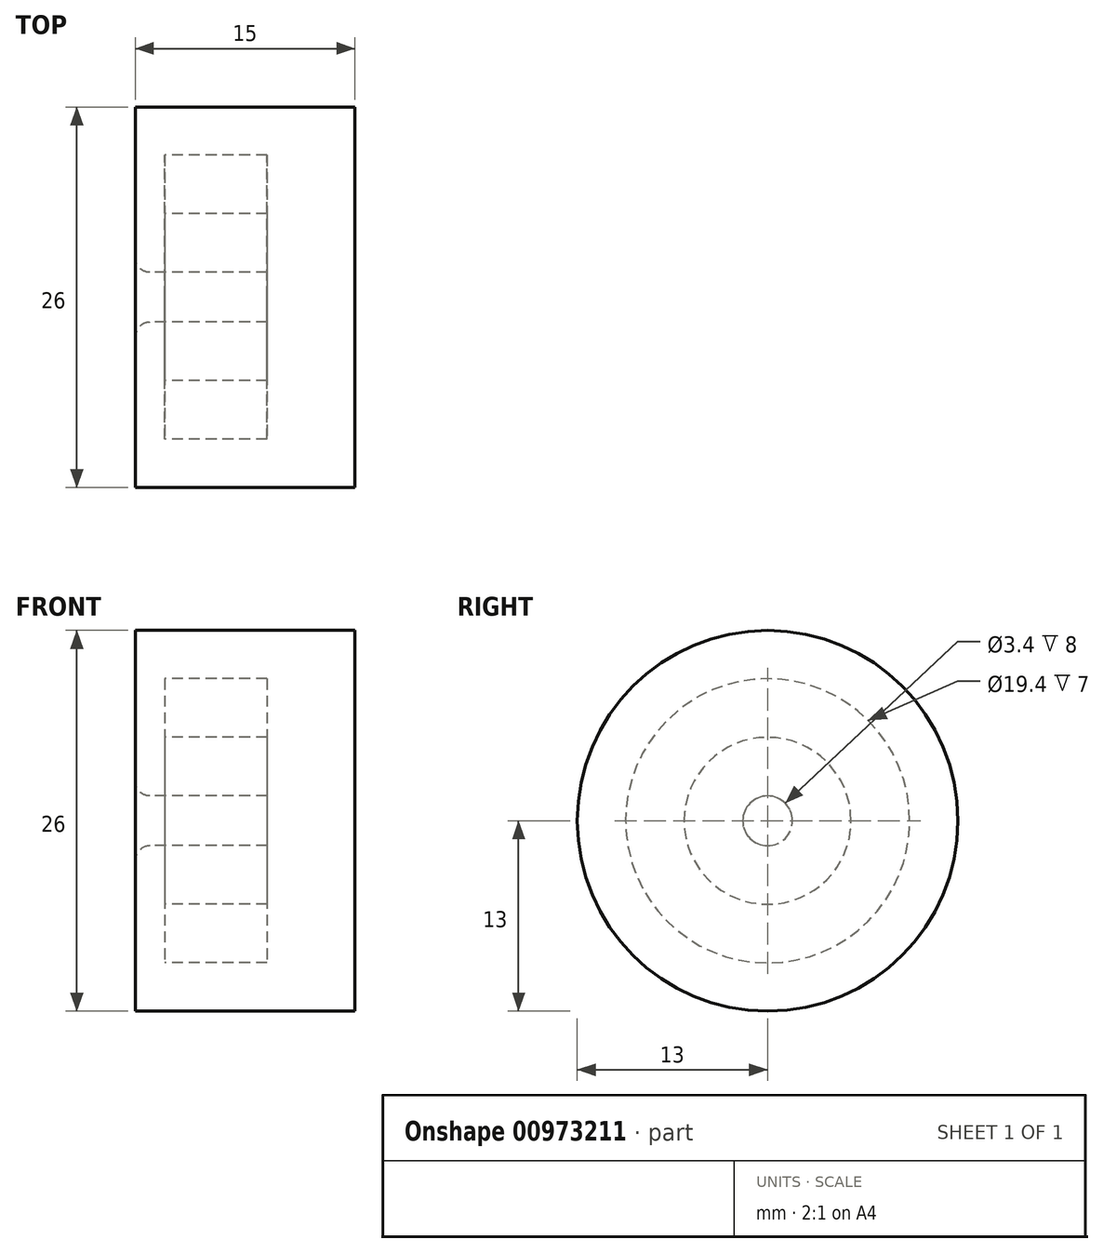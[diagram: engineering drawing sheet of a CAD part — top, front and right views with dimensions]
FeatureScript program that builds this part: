
annotation { "Feature Type Name" : "Feature", "Feature Type Description" : "" }
export const myFeature = defineFeature(function(context is Context, id is Id, definition is map)
    precondition{}
    {
        {
            var Q0;
            Q0=qCreatedBy(makeId("Front.planeOp"),FACE);
            var sketch = newSketch(context, id + "F0", { "sketchPlane" : qUnion([Q0])});
            skLineSegment(sketch, "E0", {"start": v(0, 13) * mm, "end": v(15, 13) * mm});
            skLineSegment(sketch, "E1", {"start": v(15, 13) * mm, "end": v(15, 0) * mm});
            skLineSegment(sketch, "E2", {"start": v(0, 5.7) * mm, "end": v(9, 5.7) * mm});
            skLineSegment(sketch, "E3", {"start": v(9, 5.7) * mm, "end": v(9, 9.7) * mm});
            skLineSegment(sketch, "E4", {"start": v(9, 9.7) * mm, "end": v(0, 9.7) * mm});
            skLineSegment(sketch, "E5", {"start": v(0, 13) * mm, "end": v(0, 9.7) * mm});
            skLineSegment(sketch, "E6", {"start": v(0, 1.7) * mm, "end": v(9, 1.7) * mm});
            skLineSegment(sketch, "E7", {"start": v(9, 1.7) * mm, "end": v(9, 0) * mm});
            skLineSegment(sketch, "E8", {"start": v(0, 5.7) * mm, "end": v(0, 1.7) * mm});
            skLineSegment(sketch, "E9", {"start": v(9, 0) * mm, "end": v(15, 0) * mm});
            skLineSegment(sketch, "E10", {"start": v(0, 0) * mm, "end": v(15, 0) * mm, "construction": true});
            skLineSegment(sketch, "E11", {"start": v(0, 9.7) * mm, "end": v(0, 5.7) * mm});
            skLineSegment(sketch, "E12", {"start": v(2, 9.7) * mm, "end": v(0, 9.7) * mm});
            skLineSegment(sketch, "E13", {"start": v(2, 9.7) * mm, "end": v(2, 5.7) * mm});
            skLineSegment(sketch, "E14", {"start": v(2, 5.7) * mm, "end": v(0, 5.7) * mm});
            skSolve(sketch);
        }
        {
            var Q0;
            Q0 = qSketchRegion(id + "F0", true);
            var Q1;
            Q1=sQuery(id+"F0.wireOp",EDGE,"E10");
            revolve(context, id + "F1", {"surfaceOperationType" : NewSurfaceOperationType.NEW, "entities" : qUnion([Q0]), "axis" : qUnion([Q1]), "revolveType" : RevolveType.FULL});
        }
        {
            var Q0;
            Q0=makeQuery(id+"F1.opRevolve","SWEPT_EDGE",EDGE,{"disambiguationData":[OSD([sQuery(id+"F0.wireOp",EDGE,"E6"),sQuery(id+"F0.wireOp",EDGE,"E8")])]});
            fillet(context, id + "F2", {"entities" : qUnion([Q0]), "radius" : 1 * mm, "tangentPropagation" : true, "allowEdgeOverflow" : false});
        }
    });
